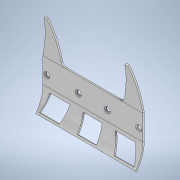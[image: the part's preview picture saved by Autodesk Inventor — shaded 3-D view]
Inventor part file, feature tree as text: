
AUTODESK INVENTOR PART (.ipt)
format: ipt  version: 2021 (Build 250183000, 183)  size: 289,792 bytes
history: native  units: mm
features: other x9, sketch x5, sheet_metal_op x1, hole x1
ambient origin geometry x8: Origin, YZ Plane, XZ Plane, XY Plane, X Axis, Y Axis, Z Axis, Center Point
bodies: Body1 (feature_tree)
feature tree (16):
  other  "Sólido1"
  sheet_metal_op  "Face1"
  other  "Dobra1"
  other  "Dobra2"
  hole  "Furo1"  [1 undecoded]
  sketch  "Esboço1"  dims[d0=100.0mm d1=90.0mm]
  other  "Placa1"
  sketch  "Esboço2"  dims[d2=1.5mm]
  sketch  "Esboço3"  dims[d3=19.0mm]
  other  "Contorno projetado1"
  sketch  "Esboço5"  dims[d4=18.0mm]
  sketch  "Esboço6"  dims[d5=2.0mm d6=15.0deg d7=2.446mm d8=20.227mm d9=1.5mm d10=0.0mm d11=1.5mm d12=0.75mm d13=3.0mm d14=1.5mm d15=6.361725mm d16=36.683mm d19=25.0mm d25=1.5mm d26=0.75mm d27=3.0mm d28=1.5mm d29=4.363323mm d30=120.0mm d31=10.0mm d32=4.0mm d33=4.0mm d34=14.5mm d35=14.5mm d36=4.0mm d37=6.0mm d38=6.0mm d39=2.0mm d40=90.0deg d41=1.5mm d42=0.0mm d46=3.0mm d47=8.0mm d48=8.0mm d49=8.0mm d50=3.0mm d51=8.0mm d52=1.5mm d53=0.0mm d54=5.0mm d55=5.0mm]
  other  "Contorno projetado5"
  other  "Contorno projetado7"
  other  "Recortar1"
  other  "Recortar3"
note: 1 required parameter value undecoded (feature->parameter linkage not recoverable at this tier; creation-order binding heuristic only, values carry confidence <= 0.55)
